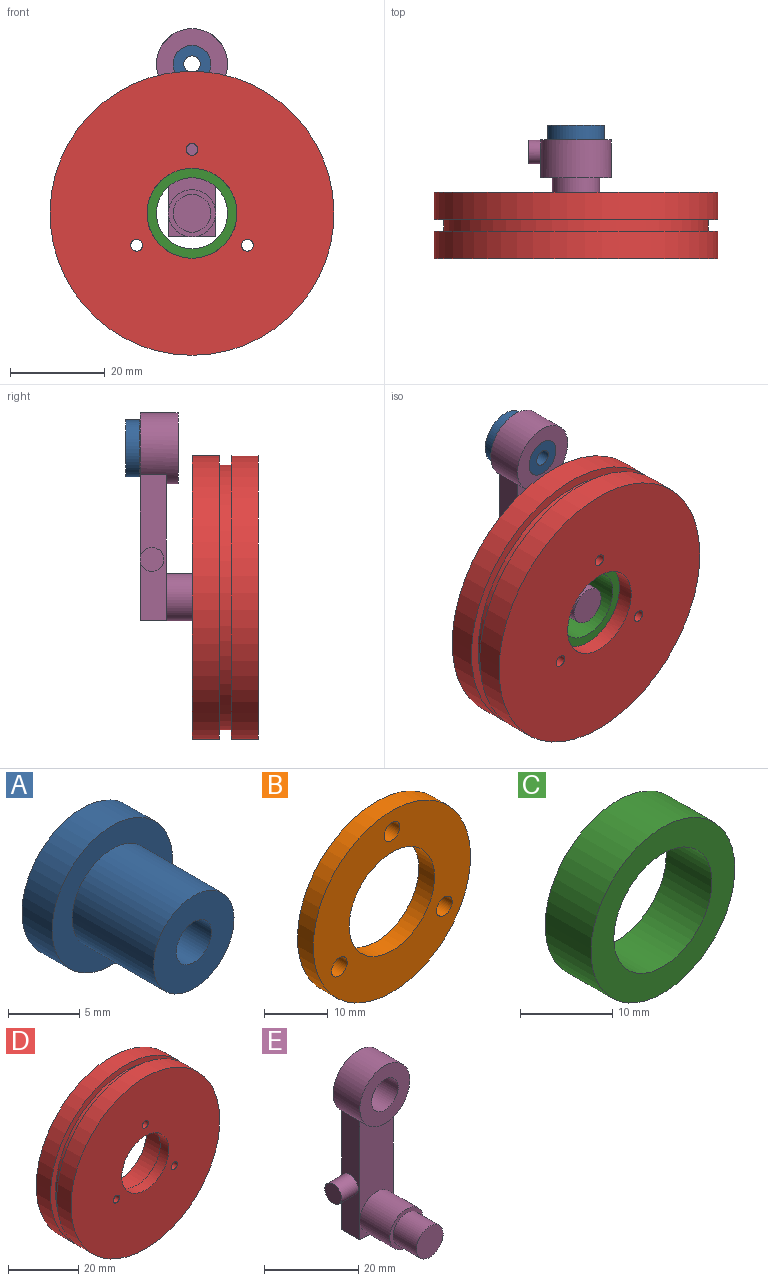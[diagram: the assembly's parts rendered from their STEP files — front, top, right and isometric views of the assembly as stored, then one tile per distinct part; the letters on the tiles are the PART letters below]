
ASSEMBLY  parts=5 mates=4
PART A: 6 faces, bbox 12x11.1x12 mm
  f0: cylinder r=4mm len=8.1mm, axis (0,1,0), area 203.6mm2, adj f1,f4
  f1: plane 8x8mm, normal (0,-1,0), area 40.6mm2, adj f0,f5
  f2: cylinder r=6mm len=12mm, axis (0,-1,0), area 113.1mm2, adj f3,f4
  f3: plane 12x12mm, normal (0,1,0), area 103.5mm2, adj f2,f5
  f4: plane 12x12mm, normal (0,-1,0), area 62.8mm2, adj f0,f2
  f5: cylinder r=1.75mm len=11.1mm, axis (0,-1,0), area 122.1mm2, adj f1,f3
PART B: 7 faces, bbox 35x3.5x35 mm
  f0: cylinder r=17.5mm len=35mm, axis (0,1,0), area 384.8mm2, adj f1,f2
  f1: plane 35x35mm, normal (0,-1,0), area 649.7mm2, adj f0,f3,f4,f5,f6
  f2: plane 35x35mm, normal (0,1,0), area 649.7mm2, adj f0,f3,f4,f5,f6
  f3: cylinder r=9.5mm len=19mm, axis (0,-1,0), area 208.9mm2, adj f1,f2
  f4: cylinder r=1.75mm len=3.5mm, axis (0,-1,0), area 38.5mm2, adj f1,f2
  f5: cylinder r=1.75mm len=3.5mm, axis (0,-1,0), area 38.5mm2, adj f1,f2
  f6: cylinder r=1.75mm len=3.5mm, axis (0,-1,0), area 38.5mm2, adj f1,f2
PART C: 4 faces, bbox 22x7x22 mm
  f0: cylinder r=7.5mm len=15mm, axis (0,1,0), area 329.9mm2, adj f2,f3
  f1: cylinder r=11mm len=22mm, axis (0,1,0), area 483.8mm2, adj f2,f3
  f2: plane 22x22mm, normal (0,-1,0), area 203.4mm2, adj f0,f1
  f3: plane 22x22mm, normal (0,1,0), area 203.4mm2, adj f0,f1
PART D: 15 faces, bbox 60x14x60 mm
  f0: cylinder r=11mm len=22mm, axis (0,1,0), area 483.8mm2, adj f8,f11
  f1: cylinder r=30mm len=60mm, axis (0,1,0), area 1083.8mm2, adj f2,f3
  f2: plane 60x60mm, normal (0,-1,0), area 2529.2mm2, adj f1,f9,f12,f13,f14
  f3: plane 60x60mm, normal (0,1,0), area 364.4mm2, adj f1,f5
  f4: plane 60x60mm, normal (0,-1,0), area 364.4mm2, adj f5,f7
  f5: cylinder r=28mm len=56mm, axis (0,-1,0), area 439.8mm2, adj f3,f4
  f6: plane 60x60mm, normal (0,1,0), area 1865.3mm2, adj f7,f10
  f7: cylinder r=30mm len=60mm, axis (0,1,0), area 1083.8mm2, adj f4,f6
  f8: plane 22x22mm, normal (0,1,0), area 96.6mm2, adj f0,f9
  f9: cylinder r=9.5mm len=19mm, axis (0,1,0), area 208.9mm2, adj f2,f8
  f10: cylinder r=17.5mm len=35mm, axis (0,1,0), area 384.8mm2, adj f6,f11
  f11: plane 35x35mm, normal (0,1,0), area 567.3mm2, adj f0,f10,f12,f13,f14
  f12: cylinder r=1.25mm len=10.5mm, axis (0,1,0), area 82.5mm2, adj f2,f11
  f13: cylinder r=1.25mm len=10.5mm, axis (0,1,0), area 82.5mm2, adj f2,f11
  f14: cylinder r=1.25mm len=10.5mm, axis (0,1,0), area 82.5mm2, adj f2,f11
PART E: 20 faces, bbox 17.5x21.5x44 mm
  f0: plane 10x5.5mm, normal (0,0,-1), area 27mm2, adj f1,f6,f7,f9,f10,f14,f15,f16
  f1: plane 44x15mm, normal (0,1,0), area 212.4mm2, adj f0,f9,f10,f11,f13,f14,f16,f17
  f2: cylinder r=4mm len=8mm, axis (0,1,0), area 175.9mm2, adj f3,f5
  f3: plane 8x8mm, normal (0,-1,0), area 50.3mm2, adj f2
  f4: cylinder r=5mm len=10mm, axis (0,-1,0), area 282.7mm2, adj f5,f6,f7,f8
  f5: plane 10x10mm, normal (0,-1,0), area 28.3mm2, adj f2,f4
  f6: plane 5x5mm, normal (0,-1,0), area 5.4mm2, adj f0,f4,f9
  f7: plane 5x5mm, normal (0,-1,0), area 5.4mm2, adj f0,f4,f10
  f8: plane 25.91x10mm, normal (0,-1,0), area 206.7mm2, adj f4,f9,f10,f11
  f9: plane 30.91x5.5mm, normal (1,0,0), area 170mm2, adj f0,f1,f6,f8,f11
  f10: plane 30.91x5.5mm, normal (-1,0,0), area 150.4mm2, adj f0,f1,f7,f8,f11,f18
  f11: cylinder r=7.5mm len=15mm, axis (0,1,0), area 316.8mm2, adj f1,f8,f9,f10,f12
  f12: plane 15x15mm, normal (0,-1,0), area 126.4mm2, adj f11,f13
  f13: cylinder r=4mm len=8mm, axis (0,1,0), area 201.1mm2, adj f1,f12
  f14: plane 30x4mm, normal (-1,0,0), area 120mm2, adj f0,f1,f15,f17
  f15: plane 30x7mm, normal (0,1,0), area 210mm2, adj f0,f14,f16,f17
  f16: plane 30x4mm, normal (1,0,0), area 120mm2, adj f0,f1,f15,f17
  f17: plane 7x4mm, normal (0,0,-1), area 28mm2, adj f1,f14,f15,f16
  f18: cylinder r=2.5mm len=5mm, axis (1,0,0), area 78.5mm2, adj f10,f19
  f19: plane 5x5mm, normal (-1,0,0), area 19.6mm2, adj f18
PLACE A t=(9.63,10.91,11.4)mm
PLACE B t=(9.63,-0.19,-20.1)mm
PLACE C t=(9.63,-3.69,-20.1)mm
PLACE D t=(9.63,-7.19,-20.1)mm
PLACE E t=(9.63,-3.69,-20.1)mm
MATE fastened A.f0 <-> E.f11  axis (0,-1,0) through (9.63,2.81,11.4)mm
MATE revolute C.f0 <-> E.f2  axis (0,1,0) through (9.63,-10.69,-20.1)mm
MATE fastened B.f0 <-> C.f1  axis (0,-1,0) through (9.63,-3.69,-20.1)mm
MATE fastened D.f0 <-> E.f2  axis (0,1,0) through (9.63,-10.69,-20.1)mm
